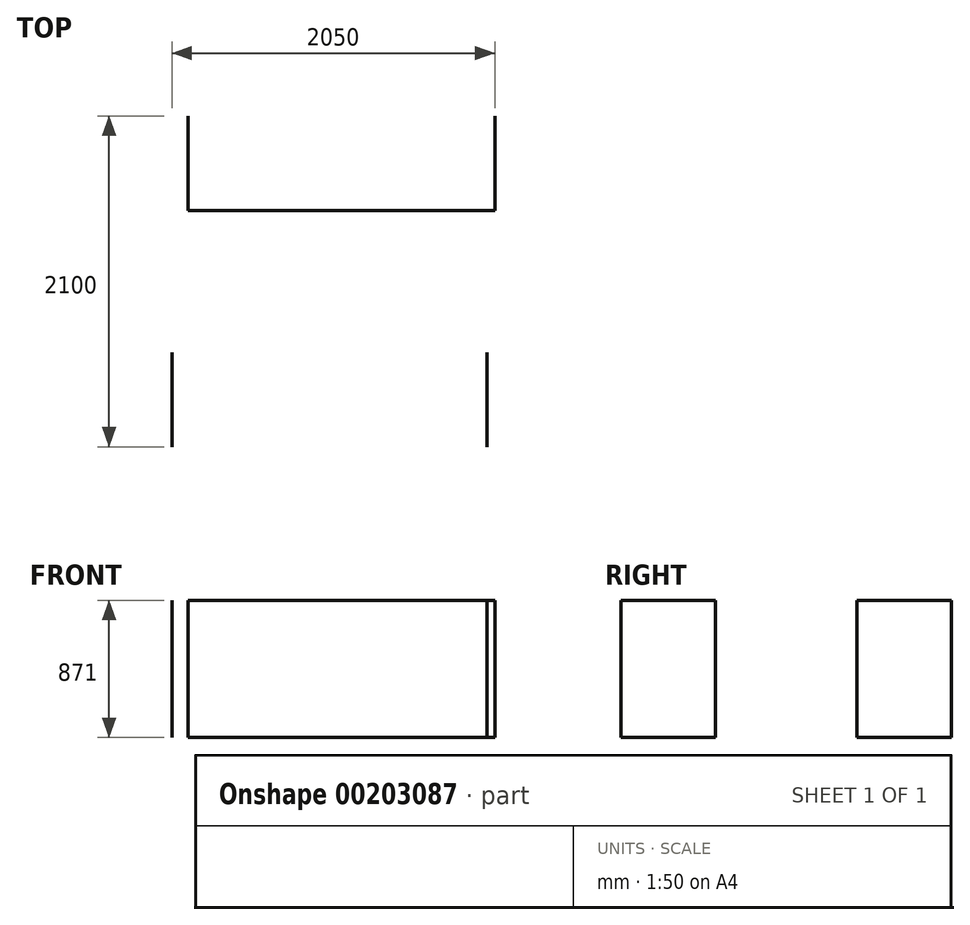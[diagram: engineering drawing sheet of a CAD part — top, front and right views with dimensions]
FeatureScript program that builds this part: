
annotation { "Feature Type Name" : "Feature", "Feature Type Description" : "" }
export const myFeature = defineFeature(function(context is Context, id is Id, definition is map)
    precondition{}
    {
        {
            var Q0;
            Q0=qCreatedBy(makeId("Top.planeOp"),FACE);
            var sketch = newSketch(context, id + "F0", { "sketchPlane" : qUnion([Q0])});
            skLineSegment(sketch, "E0.bottom", {"start": v(0, 0) * mm, "end": v(600, 0) * mm});
            skLineSegment(sketch, "E0.top", {"start": v(0, -600) * mm, "end": v(600, -600) * mm});
            skLineSegment(sketch, "E0.left", {"start": v(0, 0) * mm, "end": v(0, -600) * mm});
            skLineSegment(sketch, "E0.right", {"start": v(600, 0) * mm, "end": v(600, -600) * mm});
            skLineSegment(sketch, "E1.bottom", {"start": v(600, 0) * mm, "end": v(1050, 0) * mm});
            skLineSegment(sketch, "E1.top", {"start": v(600, -600) * mm, "end": v(1050, -600) * mm});
            skLineSegment(sketch, "E1.right", {"start": v(1050, 0) * mm, "end": v(1050, -600) * mm});
            skLineSegment(sketch, "E2.bottom", {"start": v(1050, 0) * mm, "end": v(1950, 0) * mm});
            skLineSegment(sketch, "E2.top", {"start": v(1050, -600) * mm, "end": v(1950, -600) * mm});
            skLineSegment(sketch, "E2.right", {"start": v(1950, 0) * mm, "end": v(1950, -600) * mm});
            skLineSegment(sketch, "E3.bottom", {"start": v(1950, 0) * mm, "end": v(2550, 0) * mm});
            skLineSegment(sketch, "E3.top", {"start": v(1950, -600) * mm, "end": v(2550, -600) * mm});
            skLineSegment(sketch, "E3.right", {"start": v(2550, 0) * mm, "end": v(2550, -600) * mm});
            skLineSegment(sketch, "E4.bottom", {"start": v(500, -1500) * mm, "end": v(1100, -1500) * mm});
            skLineSegment(sketch, "E4.top", {"start": v(500, -2100) * mm, "end": v(1100, -2100) * mm});
            skLineSegment(sketch, "E4.left", {"start": v(500, -1500) * mm, "end": v(500, -2100) * mm});
            skLineSegment(sketch, "E4.right", {"start": v(1100, -1500) * mm, "end": v(1100, -2100) * mm});
            skLineSegment(sketch, "E5.bottom", {"start": v(1250, -2100) * mm, "end": v(1100, -2100) * mm});
            skLineSegment(sketch, "E5.top", {"start": v(1250, -1500) * mm, "end": v(1100, -1500) * mm});
            skLineSegment(sketch, "E5.left", {"start": v(1250, -2100) * mm, "end": v(1250, -1500) * mm});
            skLineSegment(sketch, "E5.right", {"start": v(1100, -2100) * mm, "end": v(1100, -1500) * mm});
            skLineSegment(sketch, "E6.bottom", {"start": v(1250, -1500) * mm, "end": v(1750, -1500) * mm});
            skLineSegment(sketch, "E6.top", {"start": v(1250, -2100) * mm, "end": v(1750, -2100) * mm});
            skLineSegment(sketch, "E6.left", {"start": v(1250, -1500) * mm, "end": v(1250, -2100) * mm});
            skLineSegment(sketch, "E6.right", {"start": v(1750, -1500) * mm, "end": v(1750, -2100) * mm});
            skLineSegment(sketch, "E7.bottom", {"start": v(1750, -1500) * mm, "end": v(1900, -1500) * mm});
            skLineSegment(sketch, "E7.top", {"start": v(1750, -2100) * mm, "end": v(1900, -2100) * mm});
            skLineSegment(sketch, "E7.right", {"start": v(1900, -1500) * mm, "end": v(1900, -2100) * mm});
            skLineSegment(sketch, "E8.bottom", {"start": v(1900, -1500) * mm, "end": v(2500, -1500) * mm});
            skLineSegment(sketch, "E8.top", {"start": v(1900, -2100) * mm, "end": v(2500, -2100) * mm});
            skLineSegment(sketch, "E8.right", {"start": v(2500, -1500) * mm, "end": v(2500, -2100) * mm});
            skLineSegment(sketch, "E9.left", {"start": v(500, -2100) * mm, "end": v(500, -1800) * mm});
            skLineSegment(sketch, "E9.right", {"start": v(1100, -2100) * mm, "end": v(1100, -1800) * mm});
            skLineSegment(sketch, "E10.left", {"start": v(1900, -2100) * mm, "end": v(1900, -1800) * mm});
            skLineSegment(sketch, "E10.right", {"start": v(2500, -2100) * mm, "end": v(2500, -1800) * mm});
            skLineSegment(sketch, "E11.left", {"start": v(1250, -2100) * mm, "end": v(1250, -1810) * mm});
            skLineSegment(sketch, "E11.right", {"start": v(1750, -2100) * mm, "end": v(1750, -1639.45) * mm});
            skLineSegment(sketch, "E12.left", {"start": v(1250, -1810) * mm, "end": v(1250, -1667) * mm});
            skLineSegment(sketch, "E12.right", {"start": v(1750, -1639.45) * mm, "end": v(1750, -1496.45) * mm});
            skLineSegment(sketch, "E13.left", {"start": v(1250, -1667) * mm, "end": v(1250, -1592.87) * mm});
            skLineSegment(sketch, "E13.right", {"start": v(1750, -1496.45) * mm, "end": v(1750, -1417.43) * mm});
            skLineSegment(sketch, "E14.bottom", {"start": v(450, -1500) * mm, "end": v(2550, -1500) * mm});
            skLineSegment(sketch, "E14.top", {"start": v(450, -2400) * mm, "end": v(2550, -2400) * mm});
            skLineSegment(sketch, "E14.left", {"start": v(450, -1500) * mm, "end": v(450, -2400) * mm});
            skLineSegment(sketch, "E14.right", {"start": v(2550, -1500) * mm, "end": v(2550, -2400) * mm});
            skLineSegment(sketch, "E15.bottom", {"start": v(600, 0) * mm, "end": v(2550, 0) * mm});
            skLineSegment(sketch, "E15.top", {"start": v(600, -307) * mm, "end": v(2550, -307) * mm});
            skLineSegment(sketch, "E15.left", {"start": v(600, 0) * mm, "end": v(600, -307) * mm});
            skLineSegment(sketch, "E15.right", {"start": v(2550, 0) * mm, "end": v(2550, -307) * mm});
            skSolve(sketch);
        }
        {
            var Q0;
            Q0=sQuery(id+"F0.wireOp",EDGE,"E1.top");
            var Q1;
            Q1=sQuery(id+"F0.wireOp",EDGE,"E2.top");
            var Q2;
            Q2=sQuery(id+"F0.wireOp",EDGE,"E3.top");
            var Q3;
            Q3=sQuery(id+"F0.wireOp",EDGE,"E0.right");
            var Q4;
            Q4=sQuery(id+"F0.wireOp",EDGE,"E3.right");
            extrude(context, id + "F1", {"bodyType" : ToolBodyType.SURFACE, "surfaceEntities" : qUnion([Q0, Q1, Q2, Q3, Q4]), "depth" : 871 * mm});
        }
        {
            var Q0;
            Q0=sQuery(id+"F0.wireOp",EDGE,"E8.right");
            var Q1;
            Q1=sQuery(id+"F0.wireOp",EDGE,"E4.left");
            extrude(context, id + "F2", {"bodyType" : ToolBodyType.SURFACE, "surfaceEntities" : qUnion([Q0, Q1]), "depth" : 871 * mm});
        }
    });
